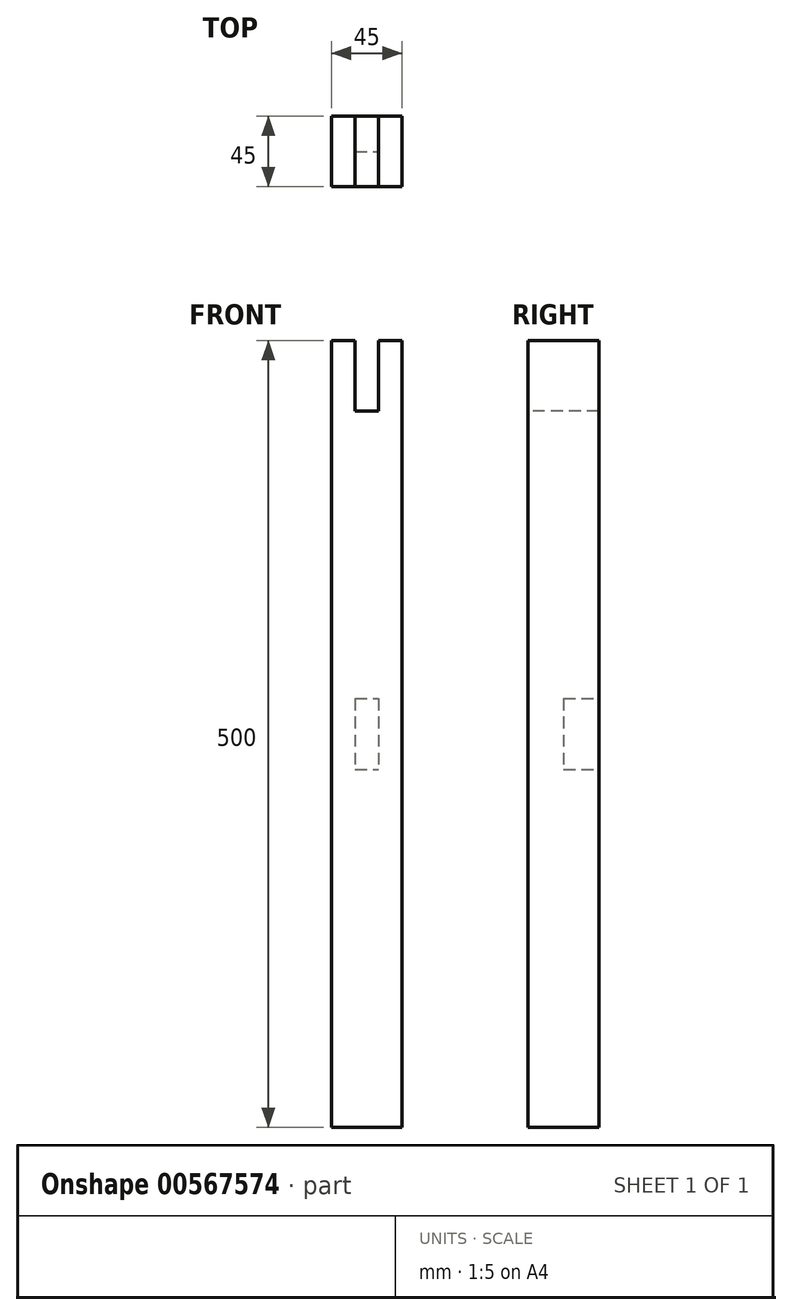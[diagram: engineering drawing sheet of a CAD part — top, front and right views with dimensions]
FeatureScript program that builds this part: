
annotation { "Feature Type Name" : "Feature", "Feature Type Description" : "" }
export const myFeature = defineFeature(function(context is Context, id is Id, definition is map)
    precondition{}
    {
        {
            var Q0;
            Q0=qCreatedBy(makeId("Front.planeOp"),FACE);
            var sketch = newSketch(context, id + "F0", { "sketchPlane" : qUnion([Q0])});
            skLineSegment(sketch, "E0.bottom", {"start": v(-22.5, 250) * mm, "end": v(22.5, 250) * mm});
            skLineSegment(sketch, "E0.top", {"start": v(-22.5, -250) * mm, "end": v(22.5, -250) * mm});
            skLineSegment(sketch, "E0.left", {"start": v(-22.5, 250) * mm, "end": v(-22.5, -250) * mm});
            skLineSegment(sketch, "E0.right", {"start": v(22.5, 250) * mm, "end": v(22.5, -250) * mm});
            skPoint(sketch, "E0.middle", {"position": v(0, 0) * mm});
            skSolve(sketch);
        }
        {
            var Q0;
            Q0=makeQuery(id+"F0.imprint","IMPRINT",FACE,{"disambiguationData":[TD([[makeQuery(id+"F0.imprint","IMPRINT",EDGE,{"derivedFrom":sQuery(id+"F0.wireOp",EDGE,"E0.bottom")}),-1.0]])]});
            extrude(context, id + "F1", {"entities" : qUnion([Q0]), "depth" : 45 * mm, "offsetDistance" : 25 * mm});
        }
        {
            var Q0;
            Q0=makeQuery(id+"F1.opExtrude","CAP_FACE",FACE,{"disambiguationData":[OSD([sQuery(id+"F0.wireOp",EDGE,"E0.bottom"),sQuery(id+"F0.wireOp",EDGE,"E0.top"),sQuery(id+"F0.wireOp",EDGE,"E0.left"),sQuery(id+"F0.wireOp",EDGE,"E0.right")])],"isStart":false});
            var sketch = newSketch(context, id + "F2", { "sketchPlane" : qUnion([Q0])});
            skLineSegment(sketch, "E1", {"start": v(-22.5, 250) * mm, "end": v(-7.5, 250) * mm});
            skLineSegment(sketch, "E2", {"start": v(22.5, 250) * mm, "end": v(7.5, 250) * mm});
            skLineSegment(sketch, "E3", {"start": v(-7.5, 250) * mm, "end": v(-7.5, 205) * mm});
            skLineSegment(sketch, "E4", {"start": v(7.5, 250) * mm, "end": v(7.5, 205) * mm});
            skLineSegment(sketch, "E5", {"start": v(-7.5, 205) * mm, "end": v(7.5, 205) * mm});
            skLineSegment(sketch, "E6", {"start": v(-7.5, 250) * mm, "end": v(7.5, 250) * mm});
            skSolve(sketch);
        }
        {
            var Q0;
            Q0=makeQuery(id+"F2.imprint","IMPRINT",FACE,{"disambiguationData":[TD([[makeQuery(id+"F2.imprint","IMPRINT",EDGE,{"derivedFrom":sQuery(id+"F2.wireOp",EDGE,"E3")}),1.0]])]});
            extrude(context, id + "F3", {"entities" : qUnion([Q0]), "operationType" : NewBodyOperationType.REMOVE, "oppositeDirection" : true, "depth" : 94 * mm, "offsetDistance" : 25 * mm});
        }
        {
            var Q0;
            Q0=qCreatedBy(makeId("Front.planeOp"),FACE);
            var sketch = newSketch(context, id + "F4", { "sketchPlane" : qUnion([Q0])});
            skLineSegment(sketch, "E7.bottom", {"start": v(-7.5, 22.5) * mm, "end": v(7.5, 22.5) * mm});
            skLineSegment(sketch, "E7.top", {"start": v(-7.5, -22.5) * mm, "end": v(7.5, -22.5) * mm});
            skLineSegment(sketch, "E7.left", {"start": v(-7.5, 22.5) * mm, "end": v(-7.5, -22.5) * mm});
            skLineSegment(sketch, "E7.right", {"start": v(7.5, 22.5) * mm, "end": v(7.5, -22.5) * mm});
            skPoint(sketch, "E7.middle", {"position": v(0, 0) * mm});
            skSolve(sketch);
        }
        {
            var Q0;
            Q0=makeQuery(id+"F4.imprint","IMPRINT",FACE,{"disambiguationData":[TD([[makeQuery(id+"F4.imprint","IMPRINT",EDGE,{"derivedFrom":sQuery(id+"F4.wireOp",EDGE,"E7.bottom")}),-1.0]])]});
            extrude(context, id + "F5", {"entities" : qUnion([Q0]), "operationType" : NewBodyOperationType.REMOVE, "depth" : 22.5 * mm, "offsetDistance" : 25 * mm});
        }
    });
